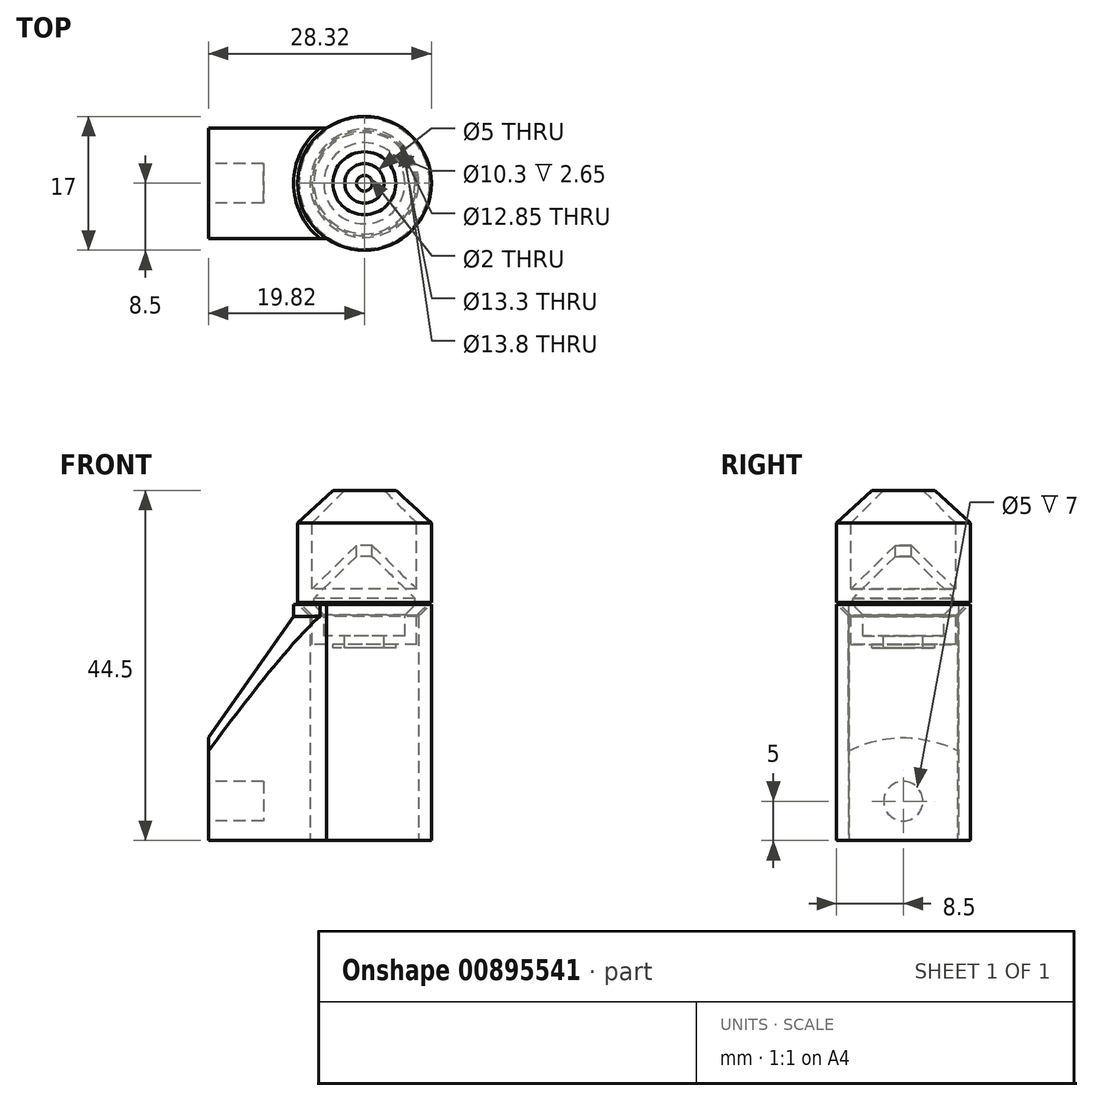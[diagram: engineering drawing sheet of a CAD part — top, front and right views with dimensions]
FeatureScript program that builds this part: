
annotation { "Feature Type Name" : "Feature", "Feature Type Description" : "" }
export const myFeature = defineFeature(function(context is Context, id is Id, definition is map)
    precondition{}
    {
        {
            var Q0;
            Q0=qCreatedBy(makeId("Top.planeOp"),FACE);
            var sketch = newSketch(context, id + "F0", { "sketchPlane" : qUnion([Q0])});
            skCircle(sketch, "E0", {"center": v(0, 0) * mm, "radius": 6.9 * mm});
            skArc(sketch, "E1", {"start": v(-4.82, -7) * mm, "mid": v(8.5, 0) * mm, "end": v(-4.82, 7) * mm});
            skLineSegment(sketch, "E2.bottom", {"start": v(-4.82, 7) * mm, "end": v(-19.82, 7) * mm});
            skLineSegment(sketch, "E2.top", {"start": v(-4.82, -7) * mm, "end": v(-19.82, -7) * mm});
            skLineSegment(sketch, "E2.right", {"start": v(-19.82, 7) * mm, "end": v(-19.82, -7) * mm});
            skSolve(sketch);
        }
        {
            var Q0;
            Q0=makeQuery(id+"F0.imprint","IMPRINT",FACE,{"disambiguationData":[TD([[makeQuery(id+"F0.imprint","IMPRINT",EDGE,{"derivedFrom":sQuery(id+"F0.wireOp",EDGE,"E0")}),-1.0]])]});
            extrude(context, id + "F1", {"entities" : qUnion([Q0]), "depth" : 30 * mm, "offsetDistance" : 25 * mm});
        }
        {
            var Q0;
            Q0=makeQuery(id+"F1.opExtrude","SWEPT_FACE",FACE,{"disambiguationData":[OSD([sQuery(id+"F0.wireOp",EDGE,"E2.right")])]});
            var sketch = newSketch(context, id + "F2", { "sketchPlane" : qUnion([Q0])});
            skCircle(sketch, "E3", {"center": v(0, 5) * mm, "radius": 2.5 * mm});
            skPoint(sketch, "E3.centerSnap0", {"position": v(0, 30) * mm});
            skPoint(sketch, "E3.centerSnap1", {"position": v(-7, 5) * mm});
            skSolve(sketch);
        }
        {
            var Q0;
            Q0=makeQuery(id+"F2.imprint","IMPRINT",FACE,{"disambiguationData":[TD([[makeQuery(id+"F2.imprint","IMPRINT",EDGE,{"derivedFrom":sQuery(id+"F2.wireOp",EDGE,"E3")}),1.0]])]});
            extrude(context, id + "F3", {"entities" : qUnion([Q0]), "operationType" : NewBodyOperationType.REMOVE, "oppositeDirection" : true, "depth" : 7 * mm, "offsetDistance" : 25 * mm});
        }
        {
            var Q0;
            Q0=makeQuery(id+"F1.opExtrude","CAP_EDGE",EDGE,{"disambiguationData":[OSD([sQuery(id+"F0.wireOp",EDGE,"E0")])],"isStart":false});
            chamfer(context, id + "F4", {"entities" : qUnion([Q0]), "width" : 1.5 * mm, "tangentPropagation" : true});
        }
        {
            var Q0;
            Q0=qCreatedBy(makeId("Front.planeOp"),FACE);
            var sketch = newSketch(context, id + "F5", { "sketchPlane" : qUnion([Q0])});
            skLineSegment(sketch, "E4.bottom", {"start": v(-23.13, 38.05) * mm, "end": v(13.03, 38.05) * mm});
            skLineSegment(sketch, "E4.top", {"start": v(-23.13, -5.22) * mm, "end": v(13.03, -5.22) * mm});
            skLineSegment(sketch, "E4.left", {"start": v(-23.13, 38.05) * mm, "end": v(-23.13, -5.22) * mm});
            skLineSegment(sketch, "E4.right", {"start": v(13.03, 38.05) * mm, "end": v(13.03, -5.22) * mm});
            skSolve(sketch);
        }
        {
            var Q0;
            Q0=qCreatedBy(makeId("Front.planeOp"),FACE);
            var sketch = newSketch(context, id + "F6", { "sketchPlane" : qUnion([Q0])});
            skLineSegment(sketch, "E5", {"start": v(-6.65, 28.6) * mm, "end": v(-8.3, 30.25) * mm});
            skLineSegment(sketch, "E6", {"start": v(-8.3, 30.25) * mm, "end": v(-8.5, 30.25) * mm});
            skLineSegment(sketch, "E7", {"start": v(-8.5, 30.25) * mm, "end": v(-8.5, 40.35) * mm});
            skLineSegment(sketch, "E8", {"start": v(-3.73, 44.5) * mm, "end": v(-2.5, 44.5) * mm});
            skLineSegment(sketch, "E9", {"start": v(-2.5, 44.5) * mm, "end": v(-6.65, 40.35) * mm});
            skLineSegment(sketch, "E10", {"start": v(-6.42, 29.92) * mm, "end": v(-6.42, 29.92) * mm});
            skLineSegment(sketch, "E11", {"start": v(-6.42, 29.92) * mm, "end": v(-5.15, 28.65) * mm});
            skLineSegment(sketch, "E12", {"start": v(0, 61.4) * mm, "end": v(0, -9.25) * mm, "construction": true});
            skLineSegment(sketch, "E13", {"start": v(-8.5, 40.35) * mm, "end": v(-4, 44.5) * mm});
            skLineSegment(sketch, "E14", {"start": v(-4, 44.5) * mm, "end": v(-3.73, 44.5) * mm});
            skLineSegment(sketch, "E15", {"start": v(-6.65, 28.6) * mm, "end": v(-6.65, 24.9) * mm});
            skLineSegment(sketch, "E16", {"start": v(-6.65, 24.5) * mm, "end": v(-6.65, 24.5) * mm});
            skLineSegment(sketch, "E17", {"start": v(-4, 24.5) * mm, "end": v(-2.5, 24.5) * mm});
            skLineSegment(sketch, "E18", {"start": v(-2.5, 24.5) * mm, "end": v(-2.5, 26) * mm});
            skPoint(sketch, "E19.orphan", {"position": v(-4.05, 26) * mm});
            skLineSegment(sketch, "E20", {"start": v(-2.5, 26) * mm, "end": v(-5.15, 26) * mm});
            skLineSegment(sketch, "E21", {"start": v(-5.15, 26) * mm, "end": v(-5.15, 27.33) * mm});
            skLineSegment(sketch, "E22", {"start": v(-5.15, 27.33) * mm, "end": v(-5.15, 28.65) * mm});
            skLineSegment(sketch, "E23", {"start": v(-6.65, 24.9) * mm, "end": v(-4, 24.9) * mm});
            skLineSegment(sketch, "E24", {"start": v(-4, 24.9) * mm, "end": v(-4, 24.5) * mm});
            skLineSegment(sketch, "E25", {"start": v(-6.65, 31.96) * mm, "end": v(-1, 37.5) * mm});
            skLineSegment(sketch, "E26", {"start": v(-1, 37.5) * mm, "end": v(-1, 36.1) * mm});
            skLineSegment(sketch, "E27", {"start": v(-1, 36.1) * mm, "end": v(-6.42, 30.78) * mm});
            skLineSegment(sketch, "E28.trimOffspring", {"start": v(-6.42, 30.78) * mm, "end": v(-6.42, 29.92) * mm});
            skLineSegment(sketch, "E29", {"start": v(-6.65, 40.35) * mm, "end": v(-6.65, 31.96) * mm});
            skSolve(sketch);
        }
        {
            var Q0;
            Q0 = qSketchRegion(id + "F6", true);
            var Q1;
            Q1=sQuery(id+"F6.wireOp",EDGE,"E12");
            revolve(context, id + "F7", {"surfaceOperationType" : NewSurfaceOperationType.NEW, "entities" : qUnion([Q0]), "axis" : qUnion([Q1]), "revolveType" : RevolveType.FULL});
        }
        {
            var Q0;
            Q0=qCreatedBy(makeId("Front.planeOp"),FACE);
            var sketch = newSketch(context, id + "F8", { "sketchPlane" : qUnion([Q0])});
            skLineSegment(sketch, "E30", {"start": v(-9, 31) * mm, "end": v(-9, 28.47) * mm});
            skLineSegment(sketch, "E31", {"start": v(-9, 28.47) * mm, "end": v(-22, 10) * mm});
            skLineSegment(sketch, "E32", {"start": v(-22, 10) * mm, "end": v(-22, 31.65) * mm});
            skLineSegment(sketch, "E33", {"start": v(-22, 31.65) * mm, "end": v(-22, 31.65) * mm});
            skLineSegment(sketch, "E34", {"start": v(-22, 31.65) * mm, "end": v(-9, 31) * mm});
            skLineSegment(sketch, "E35", {"start": v(0, 50.21) * mm, "end": v(0, -5.05) * mm, "construction": true});
            skSolve(sketch);
        }
        {
            var Q0;
            Q0 = qSketchRegion(id + "F8", true);
            var Q1;
            Q1=sQuery(id+"F8.wireOp",EDGE,"E35");
            revolve(context, id + "F9", {"operationType" : NewBodyOperationType.REMOVE, "surfaceOperationType" : NewSurfaceOperationType.NEW, "entities" : qUnion([Q0]), "axis" : qUnion([Q1]), "revolveType" : RevolveType.FULL, "oppositeDirection" : true});
        }
    });
